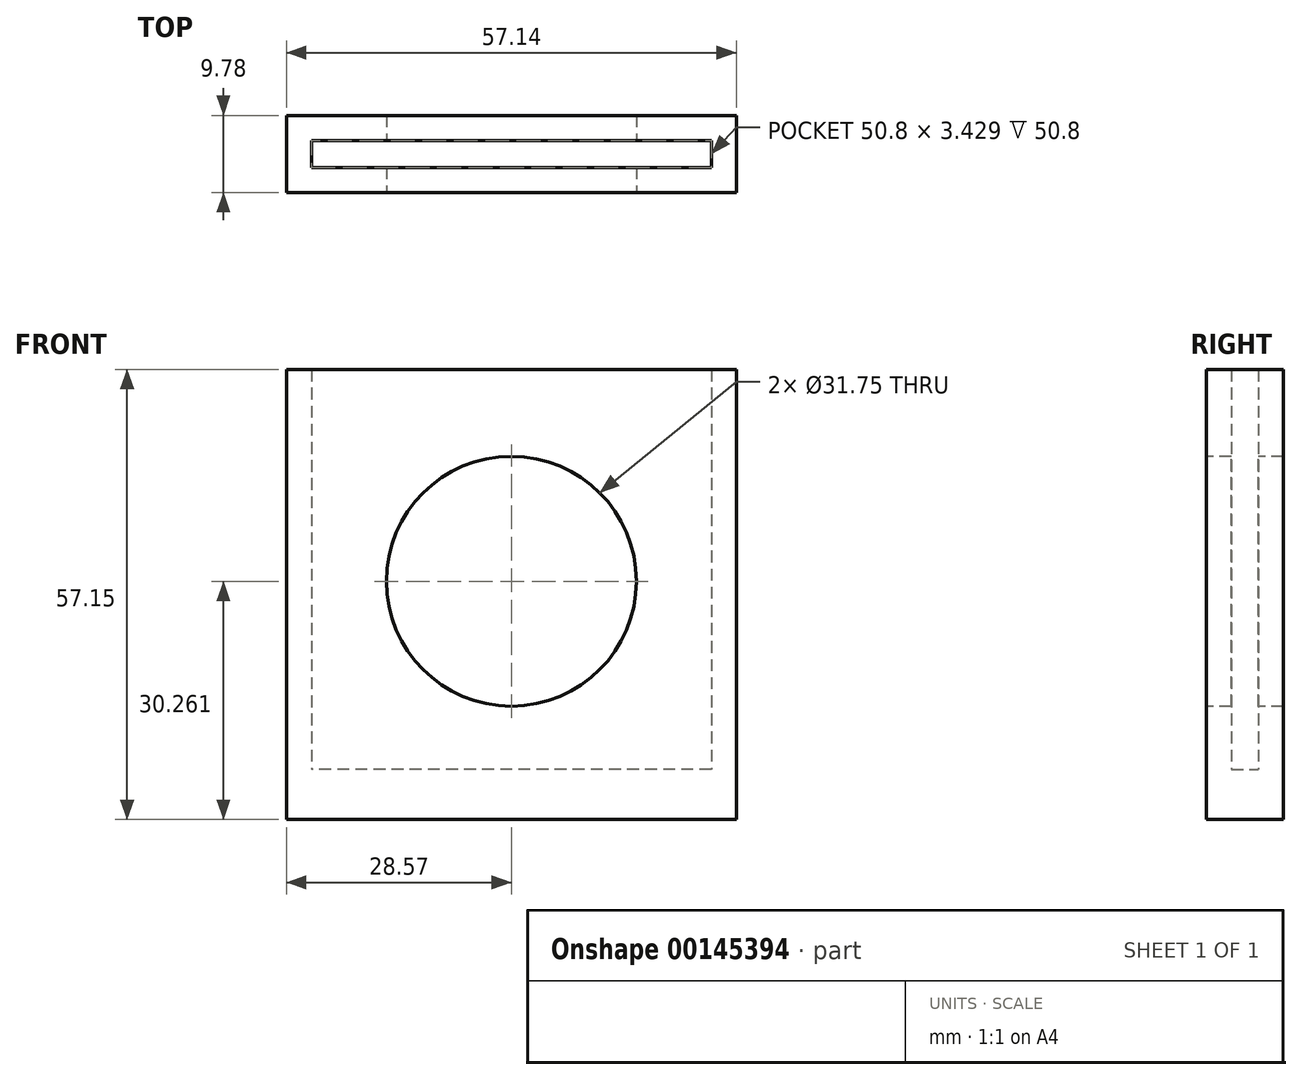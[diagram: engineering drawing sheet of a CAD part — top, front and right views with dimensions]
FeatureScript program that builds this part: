
annotation { "Feature Type Name" : "Feature", "Feature Type Description" : "" }
export const myFeature = defineFeature(function(context is Context, id is Id, definition is map)
    precondition{}
    {
        {
            var Q0;
            Q0=qCreatedBy(makeId("Top.planeOp"),FACE);
            var sketch = newSketch(context, id + "F0", { "sketchPlane" : qUnion([Q0])});
            skLineSegment(sketch, "E0.bottom", {"start": v(25.4, -1.71) * mm, "end": v(-25.4, -1.71) * mm});
            skLineSegment(sketch, "E0.top", {"start": v(25.4, 1.71) * mm, "end": v(-25.4, 1.71) * mm});
            skLineSegment(sketch, "E0.left", {"start": v(25.4, -1.71) * mm, "end": v(25.4, 1.71) * mm});
            skLineSegment(sketch, "E0.right", {"start": v(-25.4, -1.71) * mm, "end": v(-25.4, 1.71) * mm});
            skPoint(sketch, "E0.middle", {"position": v(0, 0) * mm});
            skLineSegment(sketch, "E1.0", {"start": v(28.58, 4.89) * mm, "end": v(-28.57, 4.89) * mm});
            skLineSegment(sketch, "E1.1", {"start": v(28.58, -4.89) * mm, "end": v(28.58, 4.89) * mm});
            skLineSegment(sketch, "E1.2", {"start": v(28.58, -4.89) * mm, "end": v(-28.57, -4.89) * mm});
            skLineSegment(sketch, "E1.3", {"start": v(-28.57, -4.89) * mm, "end": v(-28.57, 4.89) * mm});
            skSolve(sketch);
        }
        {
            var Q0;
            Q0=makeQuery(id+"F0.imprint","IMPRINT",FACE,{"disambiguationData":[TD([[makeQuery(id+"F0.imprint","IMPRINT",EDGE,{"derivedFrom":sQuery(id+"F0.wireOp",EDGE,"E0.bottom")}),1.0]])]});
            extrude(context, id + "F1", {"entities" : qUnion([Q0]), "depth" : 57.15 * mm});
        }
        {
            var Q0;
            Q0=makeQuery(id+"F0.imprint","IMPRINT",FACE,{"disambiguationData":[TD([[makeQuery(id+"F0.imprint","IMPRINT",EDGE,{"derivedFrom":sQuery(id+"F0.wireOp",EDGE,"E0.bottom")}),-1.0]])]});
            extrude(context, id + "F2", {"entities" : qUnion([Q0]), "operationType" : NewBodyOperationType.ADD, "depth" : 6.35 * mm});
        }
        {
            var Q0;
            Q0=makeQuery(id+"F1.opExtrude","SWEPT_FACE",FACE,{"disambiguationData":[OSD([sQuery(id+"F0.wireOp",EDGE,"E1.2")])]});
            var sketch = newSketch(context, id + "F3", { "sketchPlane" : qUnion([Q0])});
            skCircle(sketch, "E2", {"center": v(0, 30.26) * mm, "radius": 15.88 * mm});
            skPoint(sketch, "E2.centerSnap0", {"position": v(0, 57.15) * mm});
            skSolve(sketch);
        }
        {
            var Q0;
            Q0=makeQuery(id+"F3.imprint","IMPRINT",FACE,{"disambiguationData":[TD([[makeQuery(id+"F3.imprint","IMPRINT",EDGE,{"derivedFrom":sQuery(id+"F3.wireOp",EDGE,"E2")}),1.0]])]});
            var Q1;
            Q1=sQuery(id+"F3.wireOp",EDGE,"E2");
            extrude(context, id + "F4", {"entities" : qUnion([Q0]), "operationType" : NewBodyOperationType.REMOVE, "surfaceEntities" : qUnion([Q1]), "endBound" : BoundingType.THROUGH_ALL, "oppositeDirection" : true, "depth" : 25.4 * mm});
        }
    });
